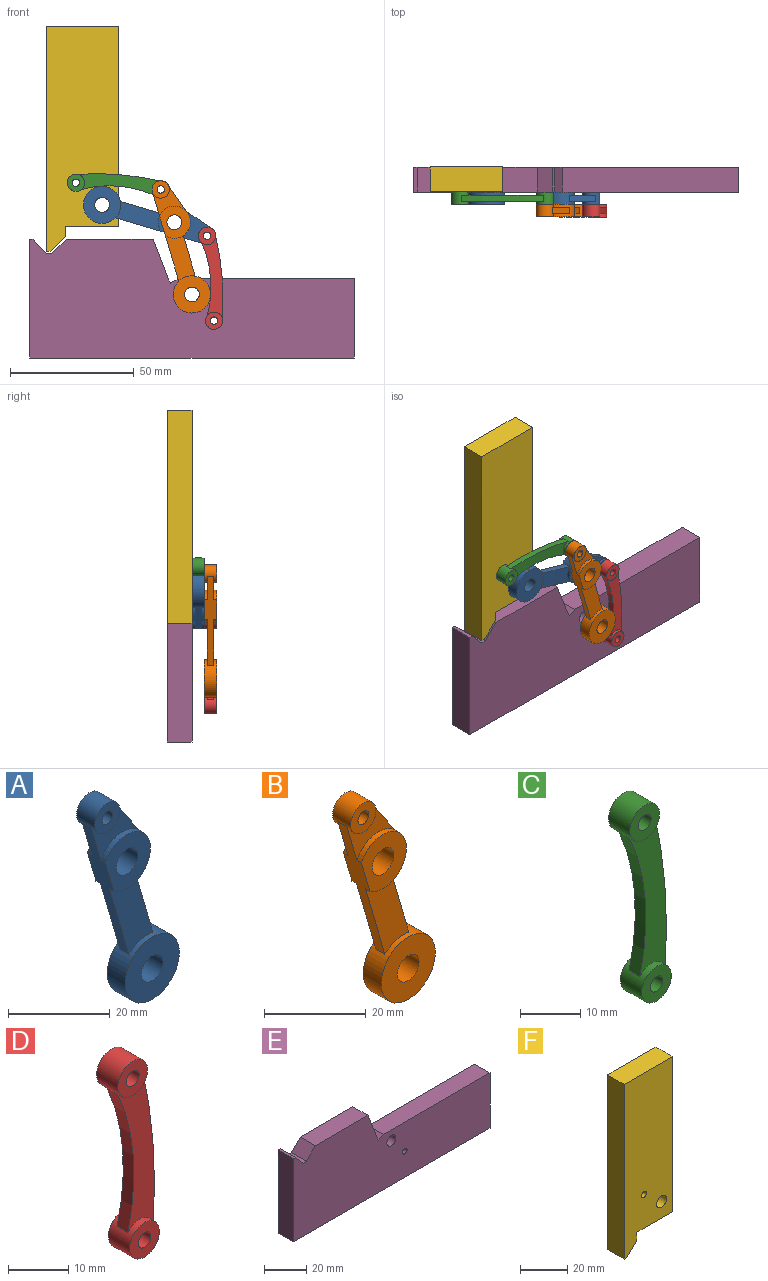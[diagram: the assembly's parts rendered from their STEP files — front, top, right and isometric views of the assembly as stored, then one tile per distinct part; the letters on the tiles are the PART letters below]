
ASSEMBLY  parts=6 mates=7
PART A: 19 faces, bbox 23.5x5x53.4 mm
  f0: cylinder r=3mm len=6mm, axis (0,1,0), area 94.2mm2, adj f2,f3
  f1: cylinder r=7.5mm len=15mm, axis (0,1,0), area 217.7mm2, adj f2,f3,f6,f16,f17,f18
  f2: plane 15x15mm, normal (0,-1,0), area 148.4mm2, adj f0,f1
  f3: plane 15x15mm, normal (0,1,0), area 148.4mm2, adj f0,f1
  f4: cylinder r=6.5mm len=13mm, axis (0,1,0), area 108.1mm2, adj f6,f7,f8,f13,f14,f15,f16,f17
  f5: cylinder r=3mm len=6mm, axis (0,1,0), area 94.2mm2, adj f7,f8
  f6: plane 35.94x10.56mm, normal (-0.96,0,-0.28), area 114.4mm2, adj f1,f4,f7,f8,f9,f14,f15,f17
  f7: plane 13x12.47mm, normal (0,-1,0), area 95.9mm2, adj f4,f5,f6
  f8: plane 13x12.47mm, normal (0,1,0), area 95.9mm2, adj f4,f5,f6
  f9: cylinder r=3.5mm len=7mm, axis (0,1,0), area 80.5mm2, adj f6,f11,f12,f13,f14,f15
  f10: cylinder r=1.5mm len=5mm, axis (0,1,0), area 47.1mm2, adj f11,f12
  f11: plane 7x7mm, normal (0,-1,0), area 31.4mm2, adj f9,f10
  f12: plane 7x7mm, normal (0,1,0), area 31.4mm2, adj f9,f10
  f13: plane 10.49x7.09mm, normal (0.83,0,0.56), area 31.6mm2, adj f4,f9,f14,f15
  f14: plane 13.43x12.46mm, normal (0,-1,0), area 53.2mm2, adj f4,f6,f9,f13
  f15: plane 13.43x12.46mm, normal (0,1,0), area 53.2mm2, adj f4,f6,f9,f13
  f16: plane 16.38x4.77mm, normal (0.96,0,0.28), area 42.6mm2, adj f1,f4,f17,f18
  f17: plane 18.38x12.01mm, normal (0,-1,0), area 116.1mm2, adj f1,f4,f6,f16
  f18: plane 18.38x12.01mm, normal (0,1,0), area 116.1mm2, adj f1,f4,f6,f16
PART B: 19 faces, bbox 23.5x5x53.4 mm
  f0: cylinder r=3mm len=6mm, axis (0,1,0), area 94.2mm2, adj f2,f3
  f1: cylinder r=7.5mm len=15mm, axis (0,1,0), area 217.7mm2, adj f2,f3,f6,f16,f17,f18
  f2: plane 15x15mm, normal (0,-1,0), area 148.4mm2, adj f0,f1
  f3: plane 15x15mm, normal (0,1,0), area 148.4mm2, adj f0,f1
  f4: cylinder r=6.5mm len=13mm, axis (0,1,0), area 108.1mm2, adj f6,f7,f8,f13,f14,f15,f16,f17
  f5: cylinder r=3mm len=6mm, axis (0,1,0), area 94.2mm2, adj f7,f8
  f6: plane 35.94x10.56mm, normal (-0.96,0,-0.28), area 114.4mm2, adj f1,f4,f7,f8,f9,f14,f15,f17
  f7: plane 13x12.47mm, normal (0,-1,0), area 95.9mm2, adj f4,f5,f6
  f8: plane 13x12.47mm, normal (0,1,0), area 95.9mm2, adj f4,f5,f6
  f9: cylinder r=3.5mm len=7mm, axis (0,1,0), area 80.5mm2, adj f6,f11,f12,f13,f14,f15
  f10: cylinder r=1.5mm len=5mm, axis (0,1,0), area 47.1mm2, adj f11,f12
  f11: plane 7x7mm, normal (0,-1,0), area 31.4mm2, adj f9,f10
  f12: plane 7x7mm, normal (0,1,0), area 31.4mm2, adj f9,f10
  f13: plane 10.49x7.09mm, normal (0.83,0,0.56), area 31.6mm2, adj f4,f9,f14,f15
  f14: plane 13.43x12.46mm, normal (0,-1,0), area 53.2mm2, adj f4,f6,f9,f13
  f15: plane 13.43x12.46mm, normal (0,1,0), area 53.2mm2, adj f4,f6,f9,f13
  f16: plane 16.38x4.77mm, normal (0.96,0,0.28), area 42.6mm2, adj f1,f4,f17,f18
  f17: plane 18.38x12.01mm, normal (0,-1,0), area 116.1mm2, adj f1,f4,f6,f16
  f18: plane 18.38x12.01mm, normal (0,1,0), area 116.1mm2, adj f1,f4,f6,f16
PART C: 12 faces, bbox 9.9x5x41.2 mm
  f0: cylinder r=3.5mm len=7mm, axis (0,1,0), area 91.5mm2, adj f2,f3,f8,f9,f10,f11
  f1: cylinder r=1.5mm len=5mm, axis (0,1,0), area 47.1mm2, adj f2,f3
  f2: plane 7x7mm, normal (0,-1,0), area 31.4mm2, adj f0,f1
  f3: plane 7x7mm, normal (0,1,0), area 31.4mm2, adj f0,f1
  f4: cylinder r=3.5mm len=7mm, axis (0,1,0), area 90.5mm2, adj f6,f7,f8,f9,f10,f11
  f5: cylinder r=1.5mm len=5mm, axis (0,1,0), area 47.1mm2, adj f6,f7
  f6: plane 7x7mm, normal (0,-1,0), area 31.4mm2, adj f4,f5
  f7: plane 7x7mm, normal (0,1,0), area 31.4mm2, adj f4,f5
  f8: cylinder r=111.22mm len=32.85mm, axis (0,1,0), area 82.7mm2, adj f0,f4,f10,f11
  f9: cylinder r=44.56mm len=29.38mm, axis (0,1,0), area 75.1mm2, adj f0,f4,f10,f11
  f10: plane 32.85x8.66mm, normal (0,-1,0), area 146.1mm2, adj f0,f4,f8,f9
  f11: plane 32.85x8.66mm, normal (0,1,0), area 146.1mm2, adj f0,f4,f8,f9
PART D: 12 faces, bbox 9.9x5x41.2 mm
  f0: cylinder r=3.5mm len=7mm, axis (0,1,0), area 91.5mm2, adj f2,f3,f8,f9,f10,f11
  f1: cylinder r=1.5mm len=5mm, axis (0,1,0), area 47.1mm2, adj f2,f3
  f2: plane 7x7mm, normal (0,-1,0), area 31.4mm2, adj f0,f1
  f3: plane 7x7mm, normal (0,1,0), area 31.4mm2, adj f0,f1
  f4: cylinder r=3.5mm len=7mm, axis (0,1,0), area 90.5mm2, adj f6,f7,f8,f9,f10,f11
  f5: cylinder r=1.5mm len=5mm, axis (0,1,0), area 47.1mm2, adj f6,f7
  f6: plane 7x7mm, normal (0,-1,0), area 31.4mm2, adj f4,f5
  f7: plane 7x7mm, normal (0,1,0), area 31.4mm2, adj f4,f5
  f8: cylinder r=111.22mm len=32.85mm, axis (0,1,0), area 82.7mm2, adj f0,f4,f10,f11
  f9: cylinder r=44.56mm len=29.38mm, axis (0,1,0), area 75.1mm2, adj f0,f4,f10,f11
  f10: plane 32.85x8.66mm, normal (0,-1,0), area 146.1mm2, adj f0,f4,f8,f9
  f11: plane 32.85x8.66mm, normal (0,1,0), area 146.1mm2, adj f0,f4,f8,f9
PART E: 16 faces, bbox 131.1x10x48 mm
  f0: plane 31.9x10mm, normal (1,0,0), area 319mm2, adj f1,f13,f14,f15
  f1: plane 71.18x10mm, normal (0,0,1), area 711.8mm2, adj f0,f2,f14,f15
  f2: plane 10x2.98mm, normal (-0.5,0,0.87), area 34.3mm2, adj f1,f3,f14,f15
  f3: plane 10x1.7mm, normal (0.87,0,0.5), area 19.6mm2, adj f2,f4,f14,f15
  f4: plane 16.07x10mm, normal (0.94,0,0.35), area 171.9mm2, adj f3,f5,f14,f15
  f5: plane 35.07x10mm, normal (0,0,1), area 350.7mm2, adj f4,f6,f14,f15
  f6: plane 10x5.97mm, normal (-0.71,0,0.71), area 84.4mm2, adj f5,f7,f14,f15
  f7: plane 10x2.19mm, normal (0,0,1), area 21.9mm2, adj f6,f8,f14,f15
  f8: plane 10x5.97mm, normal (0.75,0,0.66), area 79.4mm2, adj f7,f9,f14,f15
  f9: plane 10x1.46mm, normal (0,0,1), area 14.6mm2, adj f8,f10,f14,f15
  f10: plane 47.97x10mm, normal (-1,0,0), area 479.7mm2, adj f9,f13,f14,f15
  f11: cylinder r=1.5mm len=10mm, axis (0,1,0), area 94.2mm2, adj f14,f15
  f12: cylinder r=3mm len=10mm, axis (0,1,0), area 188.5mm2, adj f14,f15
  f13: plane 131.13x10mm, normal (0,0,-1), area 1311.3mm2, adj f0,f10,f14,f15
  f14: plane 131.13x47.97mm, normal (0,-1,0), area 4949.2mm2, adj f0,f1,f2,f3,f4,f5,f6,f7
  f15: plane 131.13x47.97mm, normal (0,1,0), area 4949.2mm2, adj f0,f1,f2,f3,f4,f5,f6,f7
PART F: 11 faces, bbox 29.1x10x90.9 mm
  f0: plane 80.76x10mm, normal (1,0,0), area 807.6mm2, adj f1,f8,f9,f10
  f1: plane 29.1x10mm, normal (0,0,1), area 291mm2, adj f0,f2,f9,f10
  f2: plane 90.86x10mm, normal (-1,0,0), area 908.6mm2, adj f1,f3,f9,f10
  f3: plane 10x1.53mm, normal (0,0,-1), area 15.3mm2, adj f2,f4,f9,f10
  f4: plane 10x6.18mm, normal (0.69,0,-0.72), area 85.9mm2, adj f3,f5,f9,f10
  f5: plane 10x4.14mm, normal (1,0,0), area 41.4mm2, adj f4,f8,f9,f10
  f6: cylinder r=3mm len=10mm, axis (0,1,0), area 188.5mm2, adj f9,f10
  f7: cylinder r=1.5mm len=10mm, axis (0,1,0), area 94.2mm2, adj f9,f10
  f8: plane 21.4x10mm, normal (0,0,-1), area 214mm2, adj f0,f5,f9,f10
  f9: plane 90.86x29.1mm, normal (0,-1,0), area 2374.1mm2, adj f0,f1,f2,f3,f4,f5,f6,f7
  f10: plane 90.86x29.1mm, normal (0,1,0), area 2374.1mm2, adj f0,f1,f2,f3,f4,f5,f6,f7
PLACE A rot(axis=(0.71,0,0.71),180deg) t=(-140.15,-12.5,14.05)mm
PLACE B rot(axis=(0,-1,0),0.2deg) t=(-146,-17.5,-0.14)mm
PLACE C rot(axis=(0,-1,0),80.8deg) t=(-75.76,-12.5,-11.18)mm
PLACE D rot(axis=(0,1,0),0deg) t=(-166.11,-17.5,0.05)mm
PLACE E at identity fixed
PLACE F rot(axis=(0,-1,0),0deg) t=(0.06,0,0.04)mm
MATE revolute C.f4 <-> F.f7  axis (0,1,0) through (-118.24,-10,77.6)mm
MATE revolute A.f0 <-> F.f6  axis (0,-1,0) through (-107.64,-10,68.68)mm
MATE revolute B.f0 <-> E.f12  axis (0,1,0) through (-71.42,-15,32.52)mm
MATE revolute A.f4 <-> B.f4  axis (0,-1,0) through (-78.5,-15,61.65)mm
MATE revolute D.f4 <-> A.f9  axis (0,1,0) through (-65.26,-15,56.18)mm
MATE revolute C.f0 <-> B.f9  axis (0,-1,0) through (-83.99,-15,74.87)mm
MATE revolute D.f0 <-> E.f11  axis (0,1,0) through (-62.48,-15,21.93)mm
